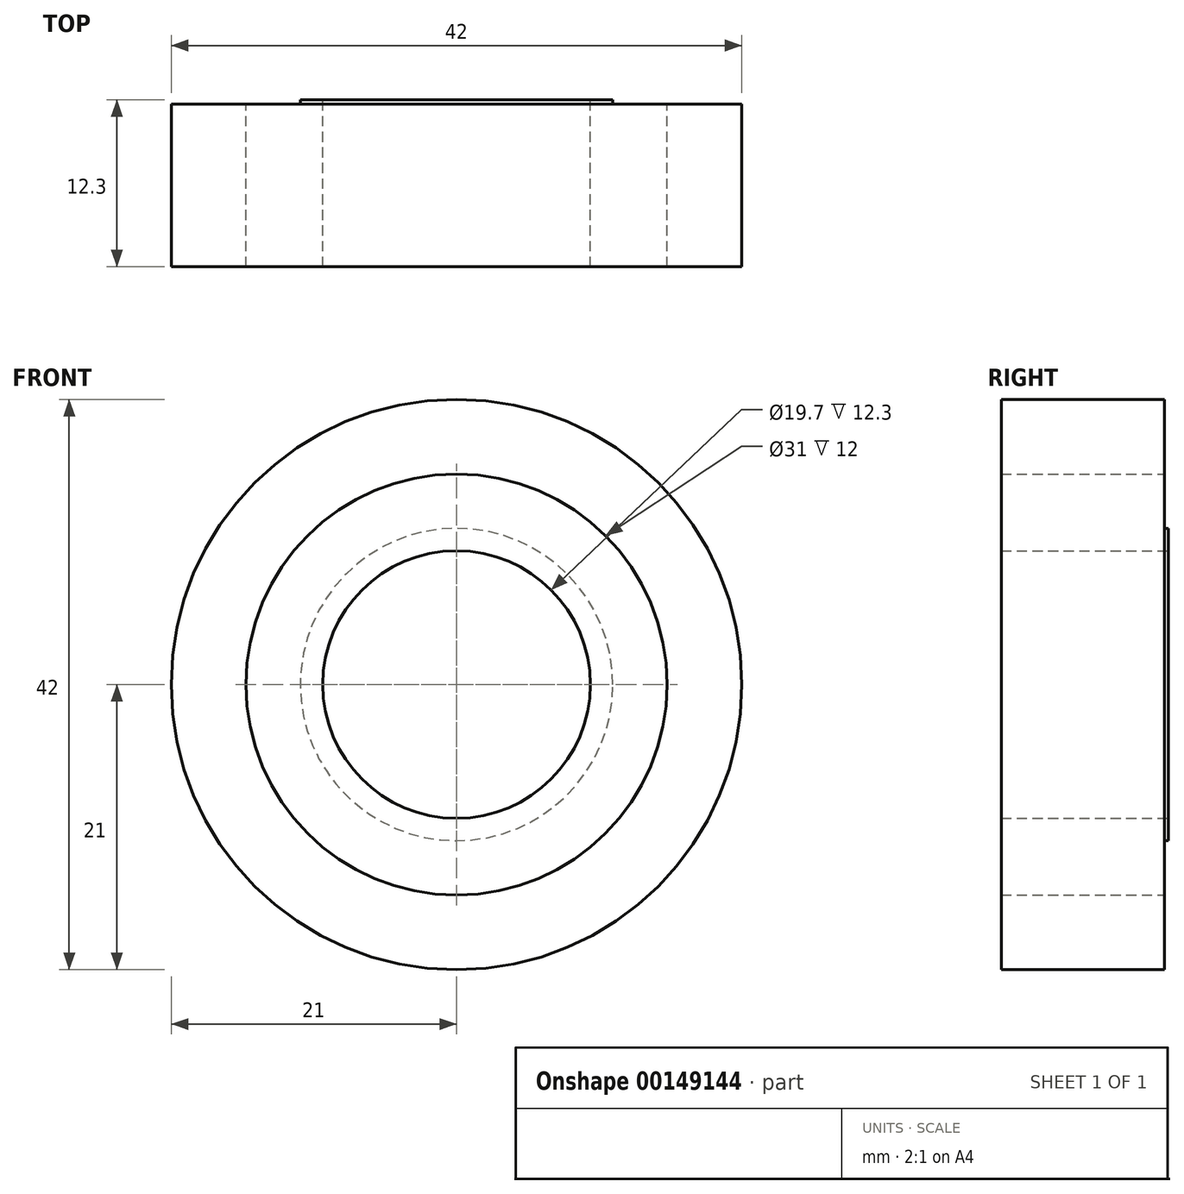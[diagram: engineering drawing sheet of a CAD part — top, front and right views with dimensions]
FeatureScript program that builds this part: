
annotation { "Feature Type Name" : "Feature", "Feature Type Description" : "" }
export const myFeature = defineFeature(function(context is Context, id is Id, definition is map)
    precondition{}
    {
        {
            var Q0;
            Q0=qCreatedBy(makeId("Front.planeOp"),FACE);
            var sketch = newSketch(context, id + "F0", { "sketchPlane" : qUnion([Q0])});
            skCircle(sketch, "E0", {"center": v(0, 0) * mm, "radius": 21 * mm});
            skCircle(sketch, "E1", {"center": v(0, 0) * mm, "radius": 10 * mm});
            skCircle(sketch, "E2", {"center": v(0, 0) * mm, "radius": 15.5 * mm});
            skSolve(sketch);
        }
        {
            var Q0;
            Q0=makeQuery(id+"F0.imprint","IMPRINT",FACE,{"disambiguationData":[TD([[makeQuery(id+"F0.imprint","IMPRINT",EDGE,{"derivedFrom":sQuery(id+"F0.wireOp",EDGE,"E0")}),1.0]])]});
            extrude(context, id + "F1", {"entities" : qUnion([Q0]), "depth" : 12 * mm});
        }
        {
            var Q0;
            Q0=makeQuery(id+"F0.imprint","IMPRINT",FACE,{"disambiguationData":[TD([[makeQuery(id+"F0.imprint","IMPRINT",EDGE,{"derivedFrom":sQuery(id+"F0.wireOp",EDGE,"E1")}),-1.0]])]});
            extrude(context, id + "F2", {"entities" : qUnion([Q0]), "depth" : 12 * mm});
        }
        {
            var Q0;
            Q0=qCreatedBy(makeId("Front.planeOp"),FACE);
            var sketch = newSketch(context, id + "F3", { "sketchPlane" : qUnion([Q0])});
            skCircle(sketch, "E3", {"center": v(0, 0) * mm, "radius": 9.85 * mm});
            skCircle(sketch, "E4", {"center": v(0, 0) * mm, "radius": 11.5 * mm});
            skCircle(sketch, "E5", {"center": v(0, 0) * mm, "radius": 10 * mm});
            skSolve(sketch);
        }
        {
            var Q0;
            Q0=makeQuery(id+"F3.imprint","IMPRINT",FACE,{"disambiguationData":[TD([[makeQuery(id+"F3.imprint","IMPRINT",EDGE,{"derivedFrom":sQuery(id+"F3.wireOp",EDGE,"E3")}),-1.0]])]});
            var Q1;
            Q1=sQuery(id+"F3.wireOp",EDGE,"E3");
            var Q2;
            Q2=sQuery(id+"F3.wireOp",EDGE,"E5");
            extrude(context, id + "F4", {"entities" : qUnion([Q0]), "surfaceEntities" : qUnion([Q1, Q2]), "depth" : 12 * mm});
        }
        {
            var Q0;
            Q0=makeQuery(id+"F3.imprint","IMPRINT",FACE,{"disambiguationData":[TD([[makeQuery(id+"F3.imprint","IMPRINT",EDGE,{"derivedFrom":sQuery(id+"F3.wireOp",EDGE,"E3")}),1.0]])]});
            var Q1;
            Q1=makeQuery(id+"F3.imprint","IMPRINT",FACE,{"disambiguationData":[TD([[makeQuery(id+"F3.imprint","IMPRINT",EDGE,{"derivedFrom":sQuery(id+"F3.wireOp",EDGE,"E3")}),-1.0]])]});
            var Q2;
            Q2=makeQuery(id+"F3.imprint","IMPRINT",FACE,{"disambiguationData":[TD([[makeQuery(id+"F3.imprint","IMPRINT",EDGE,{"derivedFrom":sQuery(id+"F3.wireOp",EDGE,"E4")}),1.0]])]});
            var Q3;
            Q3=sQuery(id+"F3.wireOp",EDGE,"E3");
            var Q4;
            Q4=sQuery(id+"F3.wireOp",EDGE,"E5");
            var Q5;
            Q5=sQuery(id+"F3.wireOp",EDGE,"E4");
            extrude(context, id + "F5", {"entities" : qUnion([Q0, Q1, Q2]), "operationType" : NewBodyOperationType.ADD, "surfaceEntities" : qUnion([Q3, Q4, Q5]), "oppositeDirection" : true, "depth" : 0.3 * mm});
        }
        {
            var Q0;
            Q0=makeQuery(id+"F3.imprint","IMPRINT",FACE,{"disambiguationData":[TD([[makeQuery(id+"F3.imprint","IMPRINT",EDGE,{"derivedFrom":sQuery(id+"F3.wireOp",EDGE,"E3")}),1.0]])]});
            extrude(context, id + "F6", {"entities" : qUnion([Q0]), "operationType" : NewBodyOperationType.REMOVE, "oppositeDirection" : true, "depth" : 25 * mm});
        }
    });
